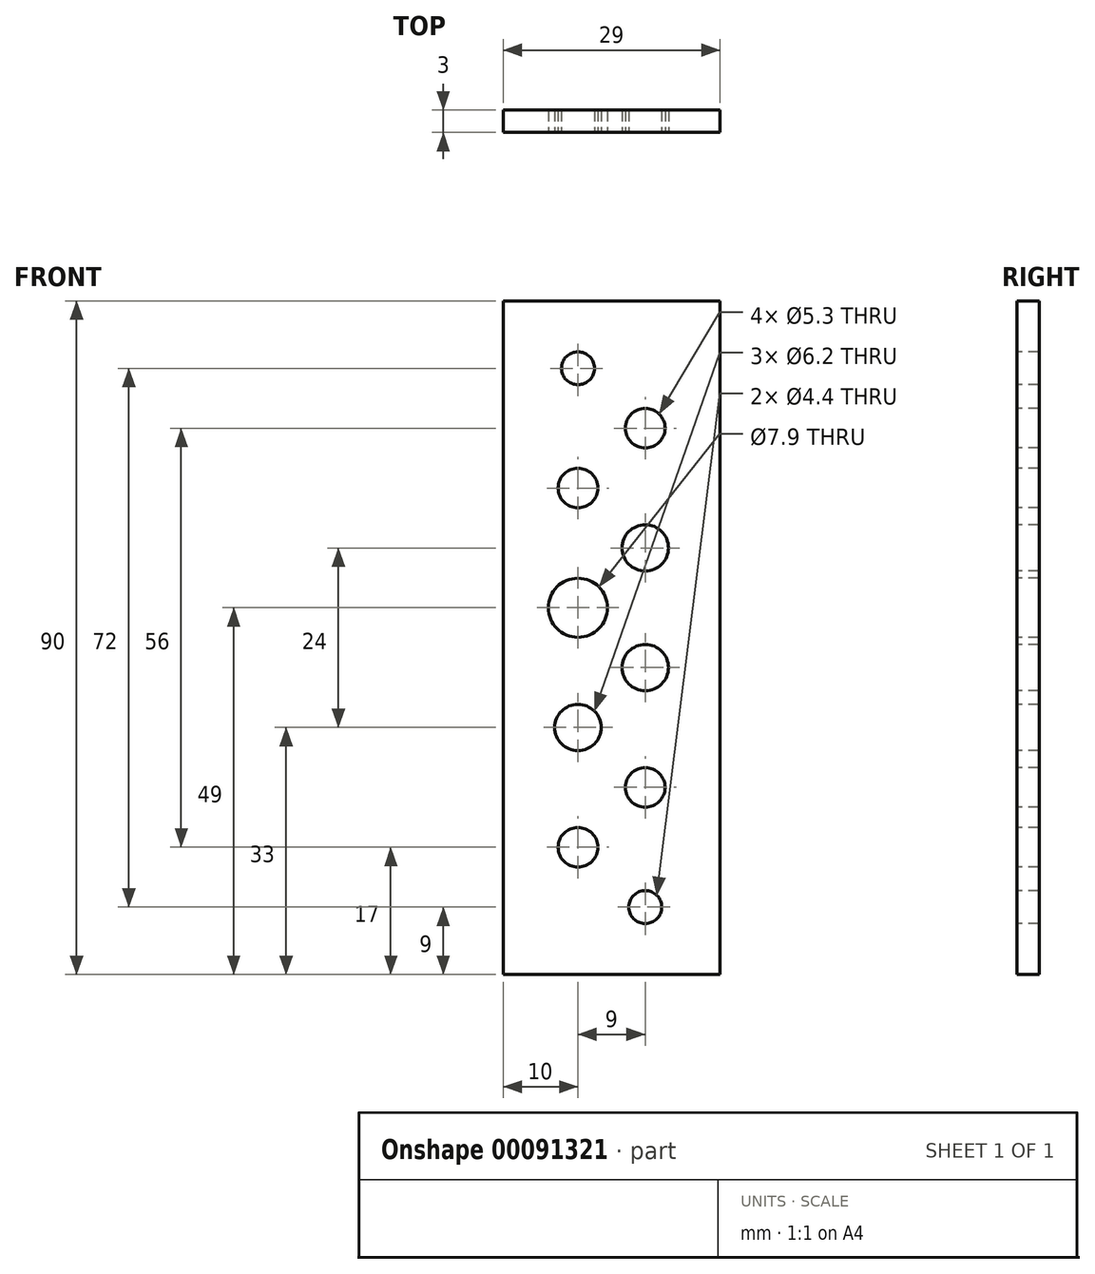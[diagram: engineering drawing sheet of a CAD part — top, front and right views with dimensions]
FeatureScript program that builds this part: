
annotation { "Feature Type Name" : "Feature", "Feature Type Description" : "" }
export const myFeature = defineFeature(function(context is Context, id is Id, definition is map)
    precondition{}
    {
        {
            var Q0;
            Q0=qCreatedBy(makeId("Front.planeOp"),FACE);
            var sketch = newSketch(context, id + "F0", { "sketchPlane" : qUnion([Q0])});
            skLineSegment(sketch, "E0.bottom", {"start": v(0, 0) * mm, "end": v(29, 0) * mm});
            skLineSegment(sketch, "E0.top", {"start": v(0, 90) * mm, "end": v(29, 90) * mm});
            skLineSegment(sketch, "E0.left", {"start": v(0, 0) * mm, "end": v(0, 90) * mm});
            skLineSegment(sketch, "E0.right", {"start": v(29, 0) * mm, "end": v(29, 90) * mm});
            skLineSegment(sketch, "E1", {"start": v(19, 90) * mm, "end": v(19, 0) * mm, "construction": true});
            skLineSegment(sketch, "E2", {"start": v(10, 90) * mm, "end": v(10, 0) * mm, "construction": true});
            skLineSegment(sketch, "E3", {"start": v(0, 81) * mm, "end": v(29, 81) * mm, "construction": true});
            skLineSegment(sketch, "E4", {"start": v(0, 73) * mm, "end": v(29, 73) * mm, "construction": true});
            skLineSegment(sketch, "E5", {"start": v(0, 65) * mm, "end": v(29, 65) * mm, "construction": true});
            skLineSegment(sketch, "E6", {"start": v(0, 57) * mm, "end": v(29, 57) * mm, "construction": true});
            skLineSegment(sketch, "E7", {"start": v(0, 49) * mm, "end": v(29, 49) * mm, "construction": true});
            skLineSegment(sketch, "E8", {"start": v(0, 41) * mm, "end": v(29, 41) * mm, "construction": true});
            skLineSegment(sketch, "E9", {"start": v(29, 33) * mm, "end": v(0, 33) * mm, "construction": true});
            skLineSegment(sketch, "E10", {"start": v(29, 25) * mm, "end": v(0, 25) * mm, "construction": true});
            skLineSegment(sketch, "E11", {"start": v(0, 17) * mm, "end": v(29, 17) * mm, "construction": true});
            skLineSegment(sketch, "E12", {"start": v(29, 9) * mm, "end": v(0, 9) * mm, "construction": true});
            skCircle(sketch, "E13", {"center": v(10, 81) * mm, "radius": 2.2 * mm});
            skCircle(sketch, "E14", {"center": v(10, 65) * mm, "radius": 2.65 * mm});
            skCircle(sketch, "E15", {"center": v(10, 49) * mm, "radius": 3.95 * mm});
            skCircle(sketch, "E16", {"center": v(10, 33) * mm, "radius": 3.1 * mm});
            skCircle(sketch, "E17", {"center": v(10, 17) * mm, "radius": 2.65 * mm});
            skCircle(sketch, "E18", {"center": v(19, 9) * mm, "radius": 2.2 * mm});
            skCircle(sketch, "E19", {"center": v(19, 25) * mm, "radius": 2.65 * mm});
            skCircle(sketch, "E20", {"center": v(19, 41) * mm, "radius": 3.1 * mm});
            skCircle(sketch, "E21", {"center": v(19, 57) * mm, "radius": 3.1 * mm});
            skCircle(sketch, "E22", {"center": v(19, 73) * mm, "radius": 2.65 * mm});
            skSolve(sketch);
        }
        {
            var Q0;
            Q0 = qSketchRegion(id + "F0", true);
            extrude(context, id + "F1", {"entities" : qUnion([Q0]), "oppositeDirection" : true, "depth" : 3 * mm});
        }
    });
